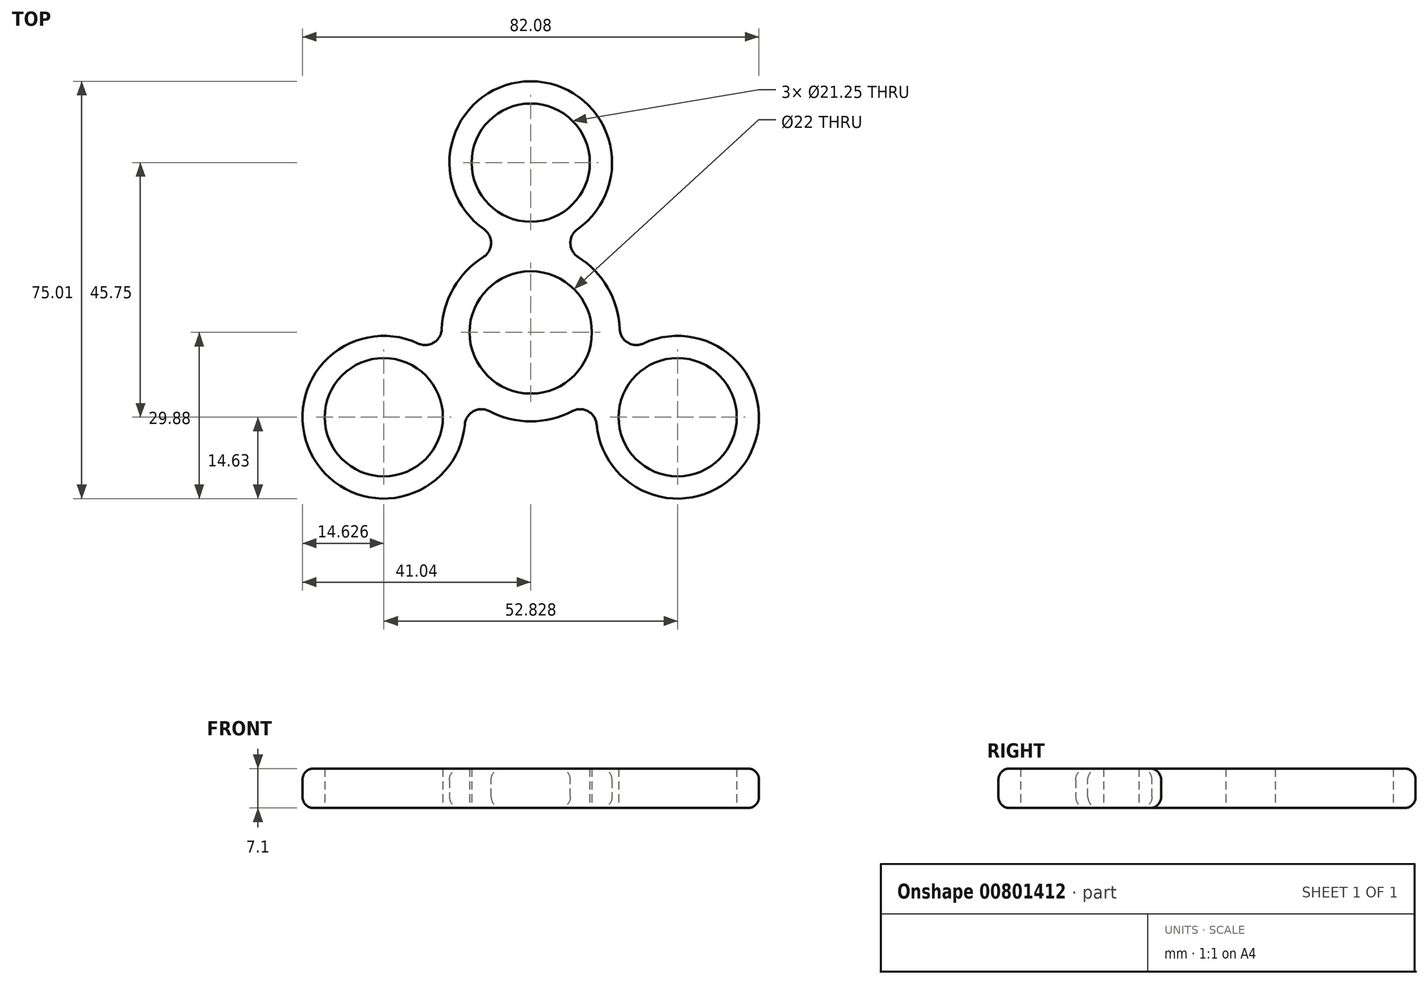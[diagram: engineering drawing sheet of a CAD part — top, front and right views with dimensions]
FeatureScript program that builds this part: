
annotation { "Feature Type Name" : "Feature", "Feature Type Description" : "" }
export const myFeature = defineFeature(function(context is Context, id is Id, definition is map)
    precondition{}
    {
        {
            var Q0;
            Q0=qCreatedBy(makeId("Top.planeOp"),FACE);
            var sketch = newSketch(context, id + "F0", { "sketchPlane" : qUnion([Q0])});
            skCircle(sketch, "E0", {"center": v(0, 0) * mm, "radius": 11 * mm});
            skCircle(sketch, "E1", {"center": v(0, 30.5) * mm, "radius": 10.62 * mm});
            skCircle(sketch, "E2", {"center": v(26.41, -15.25) * mm, "radius": 10.62 * mm});
            skCircle(sketch, "E3", {"center": v(-26.41, -15.25) * mm, "radius": 10.62 * mm});
            skCircle(sketch, "E4", {"center": v(0, 0) * mm, "radius": 30.5 * mm, "construction": true});
            skLineSegment(sketch, "E5", {"start": v(0, 0) * mm, "end": v(26.41, -15.25) * mm, "construction": true});
            skLineSegment(sketch, "E6", {"start": v(0, 0) * mm, "end": v(-26.41, -15.25) * mm, "construction": true});
            skCircle(sketch, "E7", {"center": v(0, 0) * mm, "radius": 16 * mm});
            skCircle(sketch, "E8", {"center": v(26.41, -15.25) * mm, "radius": 14.62 * mm});
            skCircle(sketch, "E9", {"center": v(-26.41, -15.25) * mm, "radius": 14.62 * mm});
            skCircle(sketch, "E10", {"center": v(0, 30.5) * mm, "radius": 14.62 * mm});
            skSolve(sketch);
        }
        {
            var Q0;
            Q0 = qSketchRegion(id + "F0", true);
            extrude(context, id + "F1", {"entities" : qUnion([Q0]), "depth" : 7.1 * mm, "offsetDistance" : 25 * mm});
        }
        {
            var Q0;
            {var subQ0=sQuery(id+"F0.wireOp",EDGE,"E9");var subQ1=sQuery(id+"F0.wireOp",EDGE,"E7");Q0=makeQuery(id+"F1.opExtrude","SWEPT_EDGE",EDGE,{"disambiguationData":[OSD([subQ1,subQ0]),TDD([makeQuery(id+"F0.imprint","INTERSECT",VERTEX,{"disambiguationData":[OD(1.0)],"derivedFrom":[subQ1,subQ0]})])]});}
            var Q1;
            {var subQ0=sQuery(id+"F0.wireOp",EDGE,"E8");var subQ1=sQuery(id+"F0.wireOp",EDGE,"E7");Q1=makeQuery(id+"F1.opExtrude","SWEPT_EDGE",EDGE,{"disambiguationData":[OSD([subQ1,subQ0]),TDD([makeQuery(id+"F0.imprint","INTERSECT",VERTEX,{"disambiguationData":[OD(0.0)],"derivedFrom":[subQ1,subQ0]})])]});}
            var Q2;
            {var subQ0=sQuery(id+"F0.wireOp",EDGE,"E8");var subQ1=sQuery(id+"F0.wireOp",EDGE,"E7");Q2=makeQuery(id+"F1.opExtrude","SWEPT_EDGE",EDGE,{"disambiguationData":[OSD([subQ1,subQ0]),TDD([makeQuery(id+"F0.imprint","INTERSECT",VERTEX,{"disambiguationData":[OD(1.0)],"derivedFrom":[subQ1,subQ0]})])]});}
            var Q3;
            {var subQ0=sQuery(id+"F0.wireOp",EDGE,"E10");var subQ1=sQuery(id+"F0.wireOp",EDGE,"E7");Q3=makeQuery(id+"F1.opExtrude","SWEPT_EDGE",EDGE,{"disambiguationData":[OSD([subQ1,subQ0]),TDD([makeQuery(id+"F0.imprint","INTERSECT",VERTEX,{"disambiguationData":[OD(1.0)],"derivedFrom":[subQ1,subQ0]})])]});}
            var Q4;
            {var subQ0=sQuery(id+"F0.wireOp",EDGE,"E10");var subQ1=sQuery(id+"F0.wireOp",EDGE,"E7");Q4=makeQuery(id+"F1.opExtrude","SWEPT_EDGE",EDGE,{"disambiguationData":[OSD([subQ1,subQ0]),TDD([makeQuery(id+"F0.imprint","INTERSECT",VERTEX,{"disambiguationData":[OD(0.0)],"derivedFrom":[subQ1,subQ0]})])]});}
            var Q5;
            {var subQ0=sQuery(id+"F0.wireOp",EDGE,"E9");var subQ1=sQuery(id+"F0.wireOp",EDGE,"E7");Q5=makeQuery(id+"F1.opExtrude","SWEPT_EDGE",EDGE,{"disambiguationData":[OSD([subQ1,subQ0]),TDD([makeQuery(id+"F0.imprint","INTERSECT",VERTEX,{"disambiguationData":[OD(0.0)],"derivedFrom":[subQ1,subQ0]})])]});}
            fillet(context, id + "F2", {"entities" : qUnion([Q0, Q1, Q2, Q3, Q4, Q5]), "radius" : 3 * mm, "tangentPropagation" : true, "allowEdgeOverflow" : false});
        }
        {
            var Q0;
            Q0=makeQuery(id+"F1.opExtrude","CAP_EDGE",EDGE,{"disambiguationData":[OSD([sQuery(id+"F0.wireOp",EDGE,"E8")])],"isStart":false});
            var Q1;
            {var subQ0=sQuery(id+"F0.wireOp",EDGE,"E8");var subQ1=sQuery(id+"F0.wireOp",EDGE,"E7");Q1=makeQuery(id+"F2.opFillet","BLEND_EDGE",EDGE,{"blendedFrom":[makeQuery(id+"F1.opExtrude","SWEPT_EDGE",EDGE,{"disambiguationData":[OSD([subQ1,subQ0]),TDD([makeQuery(id+"F0.imprint","INTERSECT",VERTEX,{"disambiguationData":[OD(0.0)],"derivedFrom":[subQ1,subQ0]})])]}),makeQuery(id+"F1.opExtrude","CAP_FACE",FACE,{"disambiguationData":[OSD([sQuery(id+"F0.wireOp",EDGE,"E0"),sQuery(id+"F0.wireOp",EDGE,"E1"),sQuery(id+"F0.wireOp",EDGE,"E2"),sQuery(id+"F0.wireOp",EDGE,"E3"),subQ1,subQ0,sQuery(id+"F0.wireOp",EDGE,"E9"),sQuery(id+"F0.wireOp",EDGE,"E10")])],"isStart":true})],"blendedInto":[makeQuery(id+"F1.opExtrude","CAP_FACE",FACE,{"disambiguationData":[OSD([sQuery(id+"F0.wireOp",EDGE,"E0"),sQuery(id+"F0.wireOp",EDGE,"E1"),sQuery(id+"F0.wireOp",EDGE,"E2"),sQuery(id+"F0.wireOp",EDGE,"E3"),subQ1,subQ0,sQuery(id+"F0.wireOp",EDGE,"E9"),sQuery(id+"F0.wireOp",EDGE,"E10")])],"isStart":true})]});}
            fillet(context, id + "F3", {"entities" : qUnion([Q0, Q1]), "radius" : 2 * mm, "tangentPropagation" : true, "allowEdgeOverflow" : false});
        }
    });
